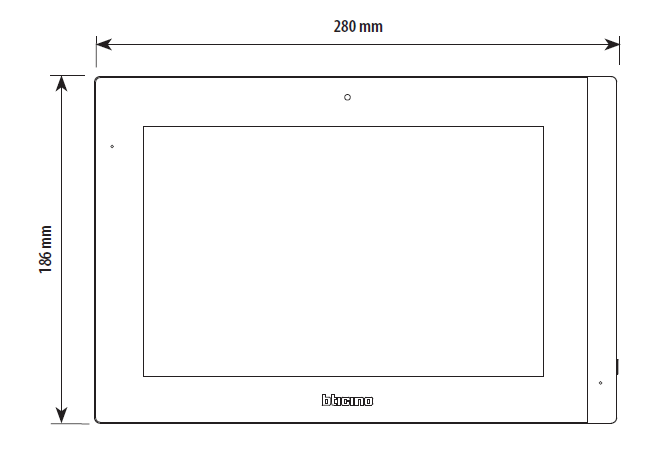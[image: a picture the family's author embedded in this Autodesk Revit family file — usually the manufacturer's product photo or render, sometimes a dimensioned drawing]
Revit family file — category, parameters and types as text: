
# Revit family: Bticino-Door Entry System-IP-Premium Indoor Unit
name_source: partatom
category: Equipement électrique
units: mm (PartAtom-declared; Revit-internal decimal feet)

## family parameters
Configuration du panneau = Deux colonnes, circuits au sein
Cote de connecteur circulaire = Utiliser le diamètre
Couper avec des vides une fois chargée = Non
Hôte = Face
Partagée = Non
Point de calcul de pièce = Non
Type d'élément = Tableau de raccordement

## types (4) — shared parameters
Color = Silver
Configurator website = https://www.homesystems-legrandgroup.com
Connected Object = Oui
Connection type = Network technology
Depth = 28 mm  [stored 0.0918635 ft]
Door open button = Oui
Elévation par défaut = 1219 mm
Fabricant = BTICINO
General Conditions of Use = https://export.legrand.com
Installation method = Hollow wall
Interface type = RJ45 Cable
Operating temperature MIN-MAX = -10/+55 °C
Tension = 24 V DC
Touchscreen = Oui

## per-type parameters (varying)
| type | Camera | Compatible with hearing aid | Height | IP | L | L1 | L3 | Product designation | Reference | Screen Size (Inch) | Visibilité cam | Width | With video | l1 | l2 |
| INDOOR UNIT 10" WITH CAMERA | With Camera | Non | 186 mm  [stored 0.610236 ft] |  | 214 mm  [stored 0.7021 ft] | 28 mm  [stored 0.0918635 ft] | 16 mm  [stored 0.0524934 ft] | IP - INDOOR UNIT WITH CAMERA 10" | BT-373001 | 10 | Oui | 280 mm  [stored 0.918635 ft] | Oui | 25 mm  [stored 0.082021 ft] | 27 mm  [stored 0.0885827 ft] |
| INDOOR UNIT 10" | Without camera | Non | 186 mm  [stored 0.610236 ft] | 30 | 214 mm  [stored 0.7021 ft] | 28 mm  [stored 0.0918635 ft] | 16 mm  [stored 0.0524934 ft] | IP - INDOOR UNIT 10" | BT-373003 | 10 | Non | 280 mm  [stored 0.918635 ft] | Non | 25 mm  [stored 0.082021 ft] | 27 mm  [stored 0.0885827 ft] |
| INDOOR UNIT 7" WITH CAMERA | With Camera | Non | 134 mm  [stored 0.439633 ft] | 30 | 155 mm  [stored 0.50853 ft] | 21 mm | 15 mm  [stored 0.0492126 ft] | IP - INDOOR UNIT WITH CAMERA 7 | BT-373002 | 7 | Oui | 211 mm  [stored 0.692257 ft] | Oui | 24 mm  [stored 0.0787402 ft] | 24 mm  [stored 0.0787402 ft] |
| INDOOR UNIT 7" | Without camera | Oui | 134 mm  [stored 0.439633 ft] | 30 | 155 mm  [stored 0.50853 ft] | 21 mm | 15 mm  [stored 0.0492126 ft] | IP - INDOOR UNIT 7" | BT-373004 | 7 | Non | 211 mm  [stored 0.692257 ft] | Non | 24 mm  [stored 0.0787402 ft] | 24 mm  [stored 0.0787402 ft] |

note: [stored X ft] marks values corroborated as IEEE doubles in the binary element streams (Revit-internal decimal feet)
